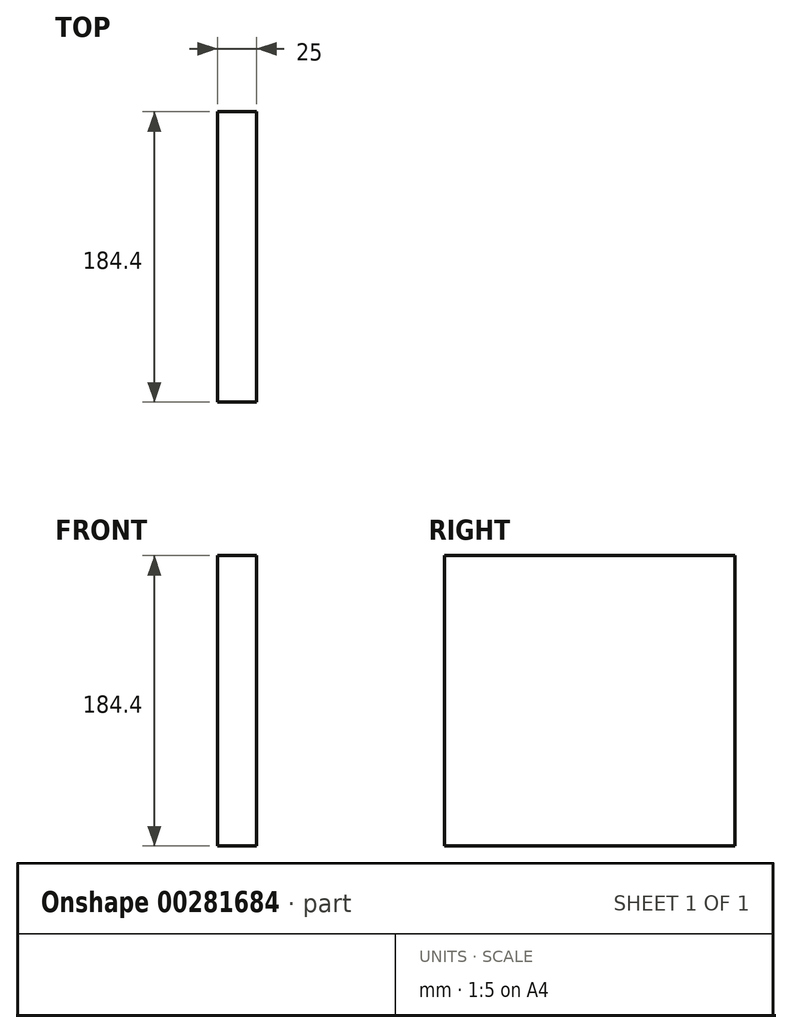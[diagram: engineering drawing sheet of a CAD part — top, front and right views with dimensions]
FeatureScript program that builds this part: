
annotation { "Feature Type Name" : "Feature", "Feature Type Description" : "" }
export const myFeature = defineFeature(function(context is Context, id is Id, definition is map)
    precondition{}
    {
        {
            var Q0;
            Q0=qCreatedBy(makeId("Right.planeOp"),FACE);
            var sketch = newSketch(context, id + "F0", { "sketchPlane" : qUnion([Q0])});
            skPoint(sketch, "E0.middle", {"position": v(0, 0) * mm});
            skLineSegment(sketch, "E1", {"start": v(-75.09, 75.09) * mm, "end": v(-40.77, 40.77) * mm});
            skLineSegment(sketch, "E2", {"start": v(-59.2, -59.42) * mm, "end": v(-40.67, -40.86) * mm});
            skLineSegment(sketch, "E3", {"start": v(-40.77, 40.77) * mm, "end": v(79.1, -79.1) * mm});
            skArc(sketch, "E4", {"start": v(40.77, 40.77) * mm, "mid": v(0, 57.65) * mm, "end": v(-40.77, 40.77) * mm});
            skArc(sketch, "E5", {"start": v(40.77, -40.77) * mm, "mid": v(57.65, 0) * mm, "end": v(40.77, 40.77) * mm});
            skLineSegment(sketch, "E6", {"start": v(-40.67, -40.86) * mm, "end": v(65.76, 65.82) * mm});
            skArc(sketch, "E7", {"start": v(-40.67, -40.86) * mm, "mid": v(0.07, -57.65) * mm, "end": v(40.77, -40.77) * mm});
            skLineSegment(sketch, "E8", {"start": v(40.77, -40.77) * mm, "end": v(40.77, -40.77) * mm});
            skLineSegment(sketch, "E9", {"start": v(40.77, 40.77) * mm, "end": v(40.77, 40.77) * mm});
            skArc(sketch, "E10", {"start": v(-40.77, 40.77) * mm, "mid": v(-57.65, -0.07) * mm, "end": v(-40.67, -40.86) * mm});
            skSolve(sketch);
        }
        {
            var Q0;
            {var subQ0=sQuery(id+"F0.wireOp",EDGE,"E10");Q0=makeQuery(id+"F0.imprint","IMPRINT",FACE,{"disambiguationData":[TD([[makeQuery(id+"F0.imprint","IMPRINT",EDGE,{"derivedFrom":subQ0}),1.0]])]});}
            cPlane(context, id + "F1", {"entities" : qUnion([Q0]), "cplaneType" : CPlaneType.OFFSET, "offset" : 100 * mm, "width" : 150 * mm, "height" : 150 * mm});
        }
        {
            var Q0;
            Q0=qCreatedBy(id+"F1.planeOp",FACE);
            var sketch = newSketch(context, id + "F2", { "sketchPlane" : qUnion([Q0])});
            skLineSegment(sketch, "E11.bottom", {"start": v(92.2, -92.2) * mm, "end": v(-92.2, -92.2) * mm});
            skLineSegment(sketch, "E11.top", {"start": v(92.2, 92.2) * mm, "end": v(-92.2, 92.2) * mm});
            skLineSegment(sketch, "E11.left", {"start": v(92.2, -92.2) * mm, "end": v(92.2, 92.2) * mm});
            skLineSegment(sketch, "E11.right", {"start": v(-92.2, -92.2) * mm, "end": v(-92.2, 92.2) * mm});
            skPoint(sketch, "E11.middle", {"position": v(0, 0) * mm});
            skSolve(sketch);
        }
        {
            var Q0;
            Q0=sQuery(id+"F2.wireOp",EDGE,"E11.top");
            var Q1;
            Q1=sQuery(id+"F0.wireOp",EDGE,"E4");
            loft(context, id + "F3", {"bodyType" : ToolBodyType.SURFACE, "wireProfilesArray" : [{ "wireProfileEntities" : qUnion([Q0]) }, { "wireProfileEntities" : qUnion([Q1]) }]});
        }
        {
            var Q0;
            Q0=makeQuery(id+"F2.imprint","IMPRINT",FACE,{"disambiguationData":[TD([[makeQuery(id+"F2.imprint","IMPRINT",EDGE,{"derivedFrom":sQuery(id+"F2.wireOp",EDGE,"E11.bottom")}),-1.0]])]});
            var Q1;
            Q1=sQuery(id+"F2.wireOp",EDGE,"E11.left");
            var Q2;
            Q2=sQuery(id+"F0.wireOp",EDGE,"E5");
            loft(context, id + "F4", {"bodyType" : ToolBodyType.SURFACE, "sheetProfilesArray" : [{ "sheetProfileEntities" : qUnion([Q0]) }], "wireProfilesArray" : [{ "wireProfileEntities" : qUnion([Q1]) }, { "wireProfileEntities" : qUnion([Q2]) }]});
        }
        {
            var Q0;
            Q0=sQuery(id+"F2.wireOp",EDGE,"E11.bottom");
            var Q1;
            Q1=sQuery(id+"F0.wireOp",EDGE,"E7");
            loft(context, id + "F5", {"bodyType" : ToolBodyType.SURFACE, "wireProfilesArray" : [{ "wireProfileEntities" : qUnion([Q0]) }, { "wireProfileEntities" : qUnion([Q1]) }]});
        }
        {
            var Q0;
            Q0=makeQuery(id+"F2.imprint","IMPRINT",FACE,{"disambiguationData":[TD([[makeQuery(id+"F2.imprint","IMPRINT",EDGE,{"derivedFrom":sQuery(id+"F2.wireOp",EDGE,"E11.bottom")}),-1.0]])]});
            var Q1;
            Q1=sQuery(id+"F2.wireOp",EDGE,"E11.right");
            var Q2;
            Q2=sQuery(id+"F0.wireOp",EDGE,"E10");
            loft(context, id + "F6", {"bodyType" : ToolBodyType.SURFACE, "sheetProfilesArray" : [{ "sheetProfileEntities" : qUnion([Q0]) }], "wireProfilesArray" : [{ "wireProfileEntities" : qUnion([Q1]) }, { "wireProfileEntities" : qUnion([Q2]) }]});
        }
        {
            var Q0;
            Q0=sQuery(id+"F0.wireOp",EDGE,"E4");
            var Q1;
            Q1=sQuery(id+"F0.wireOp",EDGE,"E10");
            var Q2;
            Q2=sQuery(id+"F0.wireOp",EDGE,"E6");
            revolve(context, id + "F7", {"bodyType" : ToolBodyType.SURFACE, "surfaceEntities" : qUnion([Q0, Q1]), "axis" : qUnion([Q2]), "revolveType" : RevolveType.FULL});
        }
        {
            var Q0;
            Q0=sQuery(id+"F2.wireOp",EDGE,"E11.left");
            var Q1;
            Q1=sQuery(id+"F2.wireOp",EDGE,"E11.bottom");
            var Q2;
            Q2=sQuery(id+"F2.wireOp",EDGE,"E11.right");
            var Q3;
            Q3=sQuery(id+"F2.wireOp",EDGE,"E11.top");
            extrude(context, id + "F8", {"bodyType" : ToolBodyType.SURFACE, "surfaceEntities" : qUnion([Q0, Q1, Q2, Q3]), "depth" : 25 * mm});
        }
        {
            var Q0;
            Q0=makeQuery(id+"F2.imprint","IMPRINT",FACE,{"disambiguationData":[TD([[makeQuery(id+"F2.imprint","IMPRINT",EDGE,{"derivedFrom":sQuery(id+"F2.wireOp",EDGE,"E11.bottom")}),-1.0]])]});
            extrude(context, id + "F9", {"entities" : qUnion([Q0]), "depth" : 25 * mm});
        }
    });
